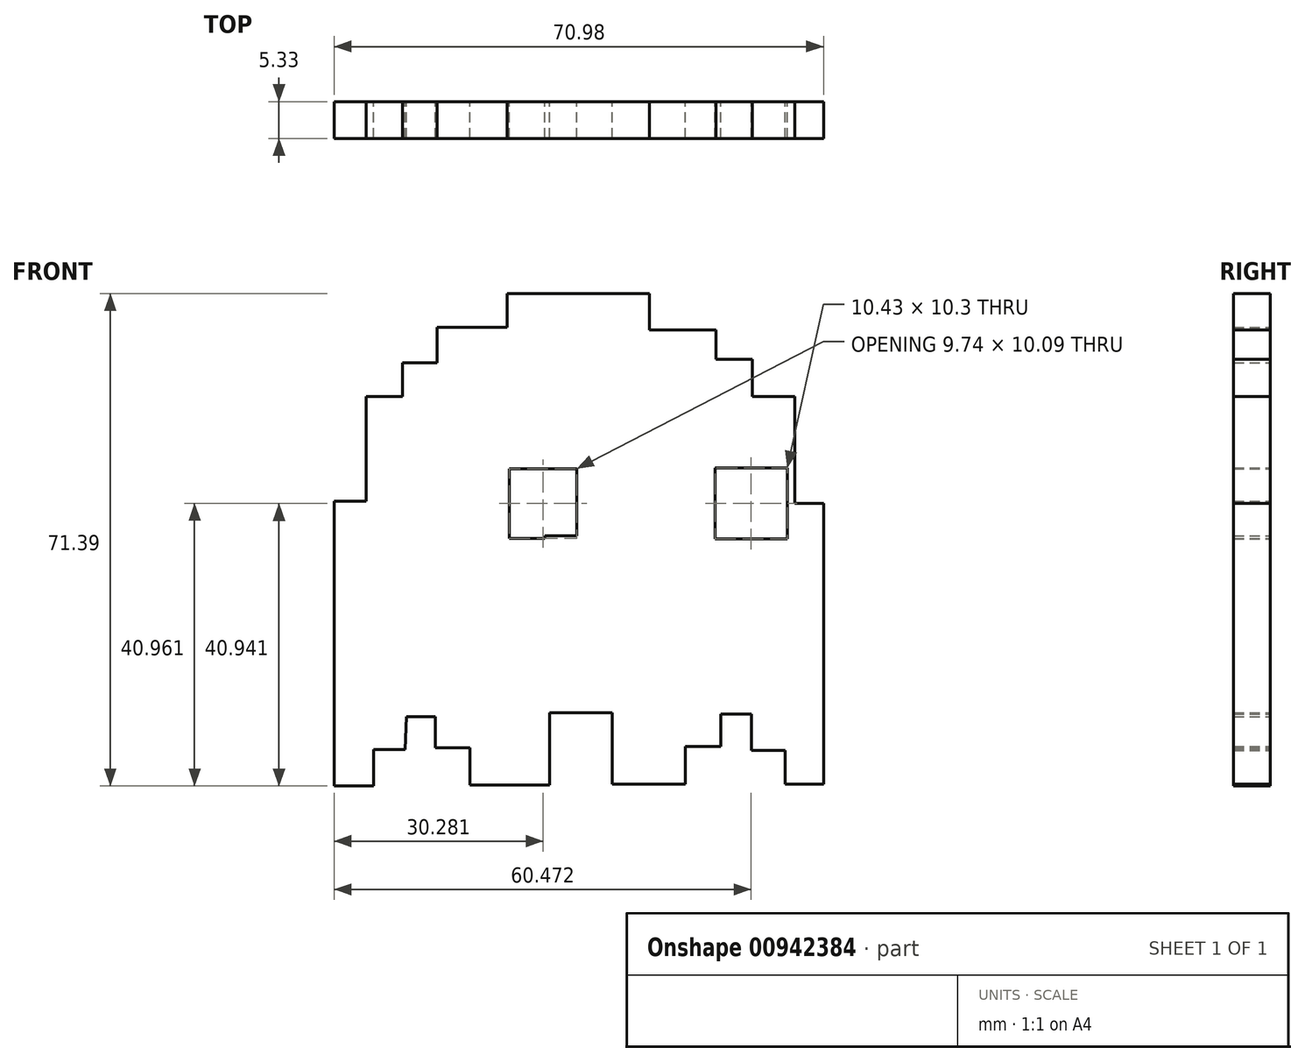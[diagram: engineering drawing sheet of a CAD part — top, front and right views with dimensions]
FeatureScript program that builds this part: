
annotation { "Feature Type Name" : "Feature", "Feature Type Description" : "" }
export const myFeature = defineFeature(function(context is Context, id is Id, definition is map)
    precondition{}
    {
        {
            var Q0;
            Q0=qCreatedBy(makeId("Front.planeOp"),FACE);
            var sketch = newSketch(context, id + "F0", { "sketchPlane" : qUnion([Q0])});
            skLineSegment(sketch, "E0", {"start": v(-28.3, -24.84) * mm, "end": v(-24.1, -24.84) * mm});
            skLineSegment(sketch, "E1", {"start": v(-24.1, -24.84) * mm, "end": v(-24.1, -29.32) * mm});
            skLineSegment(sketch, "E2", {"start": v(-24.1, -29.32) * mm, "end": v(-19.07, -29.32) * mm});
            skLineSegment(sketch, "E3", {"start": v(-19.07, -29.32) * mm, "end": v(-19.07, -34.75) * mm});
            skLineSegment(sketch, "E4", {"start": v(-19.07, -34.75) * mm, "end": v(-7.53, -34.75) * mm});
            skLineSegment(sketch, "E5", {"start": v(-7.53, -34.75) * mm, "end": v(-7.53, -24.3) * mm});
            skLineSegment(sketch, "E6", {"start": v(-7.53, -24.3) * mm, "end": v(1.56, -24.3) * mm});
            skLineSegment(sketch, "E7", {"start": v(1.56, -24.3) * mm, "end": v(1.56, -34.6) * mm});
            skLineSegment(sketch, "E8", {"start": v(1.56, -34.6) * mm, "end": v(12.15, -34.6) * mm});
            skLineSegment(sketch, "E9", {"start": v(12.15, -34.6) * mm, "end": v(12.15, -29.18) * mm});
            skLineSegment(sketch, "E10", {"start": v(12.15, -29.18) * mm, "end": v(17.3, -29.18) * mm});
            skLineSegment(sketch, "E11", {"start": v(17.3, -29.18) * mm, "end": v(17.3, -24.43) * mm});
            skLineSegment(sketch, "E12", {"start": v(17.3, -24.43) * mm, "end": v(21.78, -24.43) * mm});
            skLineSegment(sketch, "E13", {"start": v(21.78, -24.43) * mm, "end": v(21.78, -29.72) * mm});
            skLineSegment(sketch, "E14", {"start": v(21.78, -29.72) * mm, "end": v(26.67, -29.72) * mm});
            skLineSegment(sketch, "E15", {"start": v(26.67, -29.72) * mm, "end": v(26.67, -34.6) * mm});
            skLineSegment(sketch, "E16", {"start": v(26.67, -34.6) * mm, "end": v(32.23, -34.6) * mm});
            skLineSegment(sketch, "E17", {"start": v(32.23, -34.6) * mm, "end": v(32.23, 6.1) * mm});
            skLineSegment(sketch, "E18", {"start": v(32.23, 6.1) * mm, "end": v(28.03, 6.1) * mm});
            skLineSegment(sketch, "E19", {"start": v(28.03, 6.1) * mm, "end": v(28.03, 21.58) * mm});
            skLineSegment(sketch, "E20", {"start": v(28.03, 21.58) * mm, "end": v(21.92, 21.58) * mm});
            skLineSegment(sketch, "E21", {"start": v(21.92, 21.58) * mm, "end": v(21.92, 27) * mm});
            skLineSegment(sketch, "E22", {"start": v(21.92, 27) * mm, "end": v(16.63, 27) * mm});
            skLineSegment(sketch, "E23", {"start": v(16.63, 27) * mm, "end": v(16.63, 31.22) * mm});
            skLineSegment(sketch, "E24", {"start": v(16.63, 31.22) * mm, "end": v(6.99, 31.22) * mm});
            skLineSegment(sketch, "E25", {"start": v(6.99, 31.22) * mm, "end": v(6.99, 36.51) * mm});
            skLineSegment(sketch, "E26", {"start": v(6.99, 36.51) * mm, "end": v(-13.64, 36.51) * mm});
            skLineSegment(sketch, "E27", {"start": v(-13.64, 36.51) * mm, "end": v(-13.64, 31.62) * mm});
            skLineSegment(sketch, "E28", {"start": v(-13.64, 31.62) * mm, "end": v(-23.82, 31.62) * mm});
            skLineSegment(sketch, "E29", {"start": v(-23.82, 31.62) * mm, "end": v(-23.82, 26.47) * mm});
            skLineSegment(sketch, "E30", {"start": v(-23.82, 26.47) * mm, "end": v(-28.84, 26.47) * mm});
            skLineSegment(sketch, "E31", {"start": v(-28.84, 26.47) * mm, "end": v(-28.84, 21.58) * mm});
            skLineSegment(sketch, "E32", {"start": v(-28.84, 21.58) * mm, "end": v(-34.13, 21.58) * mm});
            skLineSegment(sketch, "E33", {"start": v(-34.13, 21.58) * mm, "end": v(-34.13, 6.38) * mm});
            skLineSegment(sketch, "E34", {"start": v(-34.13, 6.38) * mm, "end": v(-38.75, 6.38) * mm});
            skLineSegment(sketch, "E35", {"start": v(-38.75, 6.38) * mm, "end": v(-38.75, -34.88) * mm});
            skLineSegment(sketch, "E36", {"start": v(-38.75, -34.88) * mm, "end": v(-33.05, -34.88) * mm});
            skLineSegment(sketch, "E37", {"start": v(-33.05, -34.88) * mm, "end": v(-33.05, -29.59) * mm});
            skLineSegment(sketch, "E38", {"start": v(-33.05, -29.59) * mm, "end": v(-28.43, -29.59) * mm});
            skLineSegment(sketch, "E39", {"start": v(-28.43, -29.59) * mm, "end": v(-28.3, -24.84) * mm});
            skLineSegment(sketch, "E40", {"start": v(-18.12, 21.58) * mm, "end": v(-7.94, 21.58) * mm});
            skLineSegment(sketch, "E41", {"start": v(-7.94, 21.58) * mm, "end": v(-7.94, 16.56) * mm});
            skLineSegment(sketch, "E42", {"start": v(-7.94, 16.56) * mm, "end": v(-3.6, 16.56) * mm});
            skLineSegment(sketch, "E43", {"start": v(-3.6, 16.56) * mm, "end": v(-3.6, 1.36) * mm});
            skLineSegment(sketch, "E44", {"start": v(-3.6, 1.36) * mm, "end": v(-8.21, 1.36) * mm});
            skLineSegment(sketch, "E45", {"start": v(-8.21, 1.36) * mm, "end": v(-8.21, -3.66) * mm});
            skLineSegment(sketch, "E46", {"start": v(-8.21, -3.66) * mm, "end": v(-18.53, -3.66) * mm});
            skLineSegment(sketch, "E47", {"start": v(-18.53, -3.66) * mm, "end": v(-18.53, 1.36) * mm});
            skLineSegment(sketch, "E48", {"start": v(-18.53, 1.36) * mm, "end": v(-23.82, 1.36) * mm});
            skLineSegment(sketch, "E49", {"start": v(-23.82, 1.36) * mm, "end": v(-23.82, 16.15) * mm});
            skLineSegment(sketch, "E50", {"start": v(-23.82, 16.15) * mm, "end": v(-18.8, 16.15) * mm});
            skLineSegment(sketch, "E51", {"start": v(-18.8, 16.15) * mm, "end": v(-18.8, 21.58) * mm});
            skLineSegment(sketch, "E52", {"start": v(-18.8, 21.58) * mm, "end": v(-18.12, 21.58) * mm});
            skLineSegment(sketch, "E53", {"start": v(-13.34, 1.02) * mm, "end": v(-13.34, 11.1) * mm});
            skLineSegment(sketch, "E54", {"start": v(-13.34, 11.1) * mm, "end": v(-3.6, 11.1) * mm});
            skLineSegment(sketch, "E55", {"start": v(-3.6, 11.1) * mm, "end": v(-3.6, 1.36) * mm});
            skLineSegment(sketch, "E56", {"start": v(-13.34, 1.02) * mm, "end": v(-8.21, 1.02) * mm});
            skLineSegment(sketch, "E57", {"start": v(6.52, 15.9) * mm, "end": v(6.52, 1.1) * mm});
            skLineSegment(sketch, "E58", {"start": v(6.52, 1.1) * mm, "end": v(11.53, 1.1) * mm});
            skLineSegment(sketch, "E59", {"start": v(11.53, 1.1) * mm, "end": v(11.53, -4.2) * mm});
            skLineSegment(sketch, "E60", {"start": v(11.53, -4.2) * mm, "end": v(22.02, -4.2) * mm});
            skLineSegment(sketch, "E61", {"start": v(22.02, -4.2) * mm, "end": v(22.02, 0.93) * mm});
            skLineSegment(sketch, "E62", {"start": v(22.02, 0.93) * mm, "end": v(26.94, 0.93) * mm});
            skLineSegment(sketch, "E63", {"start": v(26.94, 0.93) * mm, "end": v(26.94, 16.22) * mm});
            skLineSegment(sketch, "E64", {"start": v(26.94, 16.22) * mm, "end": v(21.98, 16.22) * mm});
            skLineSegment(sketch, "E65", {"start": v(21.98, 16.22) * mm, "end": v(21.98, 21.27) * mm});
            skLineSegment(sketch, "E66", {"start": v(21.98, 21.27) * mm, "end": v(11.6, 21.27) * mm});
            skLineSegment(sketch, "E67", {"start": v(11.6, 21.27) * mm, "end": v(11.6, 16.18) * mm});
            skLineSegment(sketch, "E68", {"start": v(11.6, 16.18) * mm, "end": v(6.52, 16.18) * mm});
            skLineSegment(sketch, "E69", {"start": v(6.52, 16.18) * mm, "end": v(6.52, 15.9) * mm});
            skLineSegment(sketch, "E70", {"start": v(22.02, 0.93) * mm, "end": v(16.5, 0.93) * mm});
            skLineSegment(sketch, "E71", {"start": v(16.5, 0.93) * mm, "end": v(16.5, 11.23) * mm});
            skLineSegment(sketch, "E72", {"start": v(16.5, 11.23) * mm, "end": v(26.94, 11.23) * mm});
            skSolve(sketch);
        }
        {
            var Q0;
            Q0=makeQuery(id+"F0.imprint","IMPRINT",FACE,{"disambiguationData":[TD([[makeQuery(id+"F0.imprint","IMPRINT",EDGE,{"derivedFrom":sQuery(id+"F0.wireOp",EDGE,"E0")}),1.0]])]});
            var Q1;
            Q1=makeQuery(id+"F0.imprint","IMPRINT",FACE,{"disambiguationData":[TD([[makeQuery(id+"F0.imprint","IMPRINT",EDGE,{"derivedFrom":sQuery(id+"F0.wireOp",EDGE,"E40")}),-1.0]])]});
            var Q2;
            Q2=makeQuery(id+"F0.imprint","IMPRINT",FACE,{"disambiguationData":[TD([[makeQuery(id+"F0.imprint","IMPRINT",EDGE,{"derivedFrom":sQuery(id+"F0.wireOp",EDGE,"E57")}),1.0]])]});
            extrude(context, id + "F1", {"entities" : qUnion([Q0, Q1, Q2]), "depth" : 5.33 * mm, "offsetDistance" : 25.4 * mm});
        }
    });
